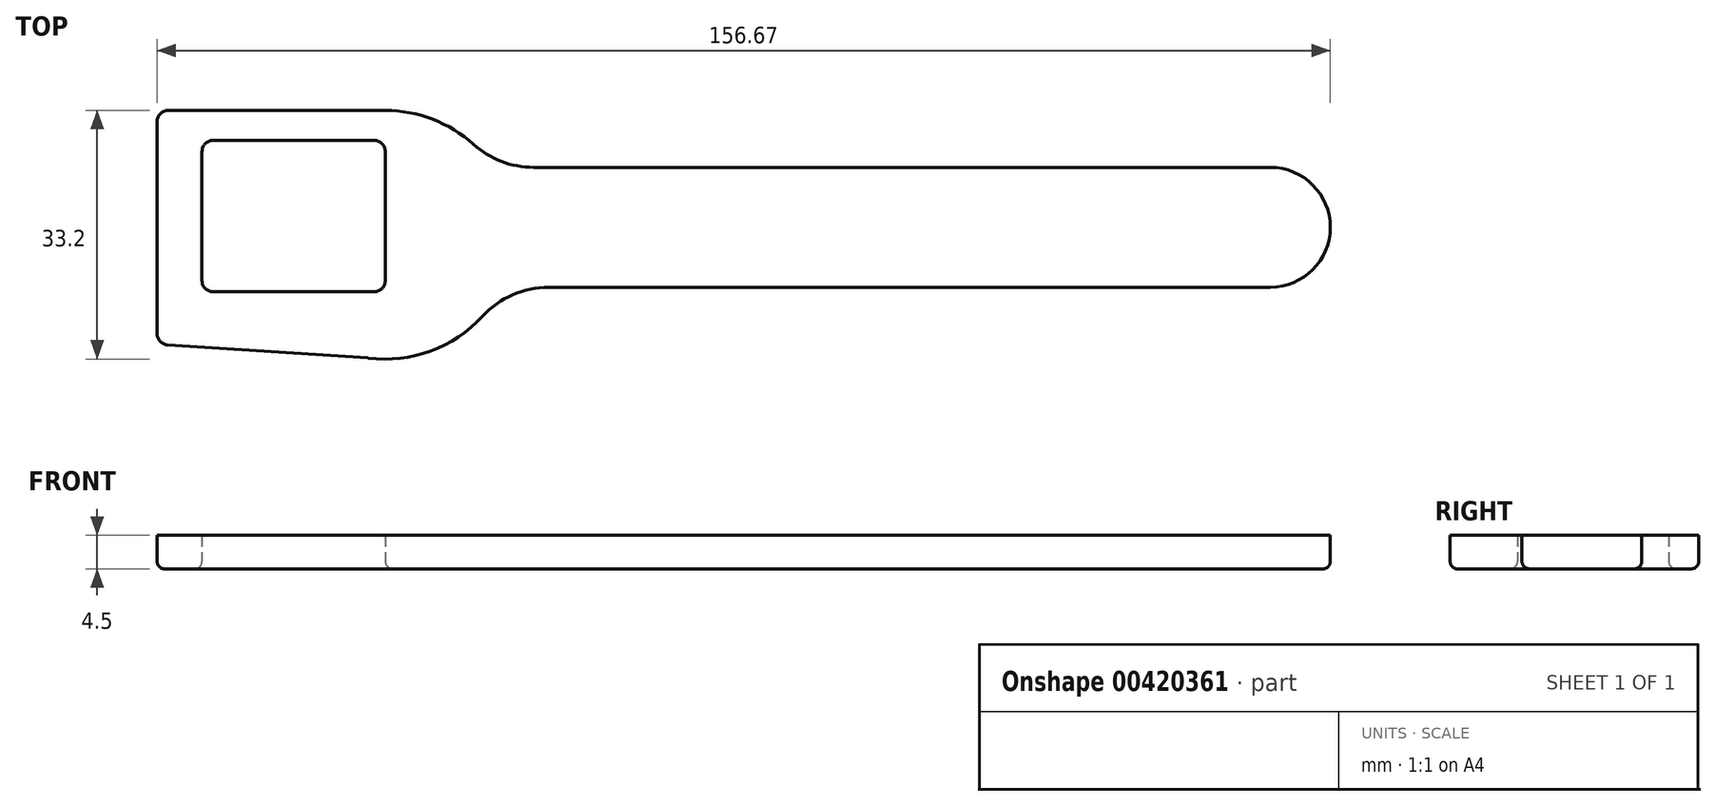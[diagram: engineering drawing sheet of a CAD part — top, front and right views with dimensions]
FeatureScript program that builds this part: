
annotation { "Feature Type Name" : "Feature", "Feature Type Description" : "" }
export const myFeature = defineFeature(function(context is Context, id is Id, definition is map)
    precondition{}
    {
        {
            var Q0;
            Q0=qCreatedBy(makeId("Top.planeOp"),FACE);
            var sketch = newSketch(context, id + "F0", { "sketchPlane" : qUnion([Q0])});
            skArc(sketch, "E0", {"start": v(-72.82, -17.45) * mm, "mid": v(-62.33, -15.58) * mm, "end": v(-54.85, -8) * mm});
            skLineSegment(sketch, "E1", {"start": v(59.4, -20.35) * mm, "end": v(59.4, 16.2) * mm, "construction": true});
            skLineSegment(sketch, "E2", {"start": v(-88.12, 35.8) * mm, "end": v(-88.12, -38.11) * mm, "construction": true});
            skLineSegment(sketch, "E3.top", {"start": v(-70.52, -17.6) * mm, "end": v(-50.32, -17.6) * mm, "construction": true});
            skLineSegment(sketch, "E3.right", {"start": v(-50.32, 17.6) * mm, "end": v(-50.32, -17.6) * mm, "construction": true});
            skLineSegment(sketch, "E4.top", {"start": v(-70.52, -8.6) * mm, "end": v(-88.12, -8.6) * mm});
            skLineSegment(sketch, "E5", {"start": v(-63.17, 15.6) * mm, "end": v(-90.72, 15.6) * mm});
            skLineSegment(sketch, "E6", {"start": v(-70.52, -17.6) * mm, "end": v(-101, -15.6) * mm});
            skLineSegment(sketch, "E7", {"start": v(-98.89, 0) * mm, "end": v(66.7, 0) * mm, "construction": true});
            skArc(sketch, "E8", {"start": v(47.67, -8) * mm, "mid": v(55.67, 0) * mm, "end": v(47.67, 8) * mm});
            skLineSegment(sketch, "E9", {"start": v(47.67, 8) * mm, "end": v(-50.32, 8) * mm});
            skLineSegment(sketch, "E10", {"start": v(47.67, -8) * mm, "end": v(-54.85, -8) * mm});
            skArc(sketch, "E11.trimOffspring", {"start": v(-56.04, 8) * mm, "mid": v(-62.35, 13.58) * mm, "end": v(-70.52, 15.6) * mm});
            skLineSegment(sketch, "E12", {"start": v(-97.29, 15.6) * mm, "end": v(-46.92, 15.6) * mm, "construction": true});
            skLineSegment(sketch, "E13", {"start": v(-50.32, 8) * mm, "end": v(-56.04, 8) * mm});
            skLineSegment(sketch, "E14.bottom", {"start": v(-90.72, 15.6) * mm, "end": v(-95, 15.6) * mm});
            skLineSegment(sketch, "E15.bottom", {"start": v(-95, 15.6) * mm, "end": v(-101, 15.6) * mm});
            skLineSegment(sketch, "E15.left", {"start": v(-95, 11.6) * mm, "end": v(-95, -8.6) * mm});
            skLineSegment(sketch, "E15.right", {"start": v(-101, 15.6) * mm, "end": v(-101, -15.6) * mm});
            skLineSegment(sketch, "E16", {"start": v(-95, 11.6) * mm, "end": v(-70.52, 11.6) * mm});
            skLineSegment(sketch, "E17", {"start": v(-88.12, -8.6) * mm, "end": v(-95, -8.6) * mm});
            skLineSegment(sketch, "E18", {"start": v(-70.52, 11.6) * mm, "end": v(-70.52, -8.6) * mm});
            skSolve(sketch);
        }
        {
            var Q0;
            Q0=qSketchRegion(id+"F0",true);
            extrude(context, id + "F1", {"entities" : qUnion([Q0]), "depth" : 4.5 * mm});
        }
        {
            var Q0;
            Q0=makeQuery(id+"F1.opExtrude","SWEPT_EDGE",EDGE,{"disambiguationData":[OSD([sQuery(id+"F0.wireOp",EDGE,"E0"),sQuery(id+"F0.wireOp",EDGE,"E6")])]});
            var Q1;
            Q1=makeQuery(id+"F1.opExtrude","SWEPT_EDGE",EDGE,{"disambiguationData":[OSD([sQuery(id+"F0.wireOp",EDGE,"E5"),sQuery(id+"F0.wireOp",EDGE,"E11.trimOffspring")])]});
            var Q2;
            Q2=makeQuery(id+"F1.opExtrude","SWEPT_EDGE",EDGE,{"disambiguationData":[OSD([sQuery(id+"F0.wireOp",EDGE,"E4.top"),sQuery(id+"F0.wireOp",EDGE,"MguvdN41-JgFZ-7uOa-Q9f6-B0BVnigIjYcD")])]});
            var Q3;
            Q3=makeQuery(id+"F1.opExtrude","SWEPT_EDGE",EDGE,{"disambiguationData":[OSD([sQuery(id+"F0.wireOp",EDGE,"E4.top"),sQuery(id+"F0.wireOp",EDGE,"MguvdN41-JgFZ-7uOa-Q9f6-B0BVnigIjYcD")])]});
            var Q4;
            Q4=makeQuery(id+"F1.opExtrude","SWEPT_EDGE",EDGE,{"disambiguationData":[OSD([sQuery(id+"F0.wireOp",EDGE,"MguvdN41-JgFZ-7uOa-Q9f6-B0BVnigIjYcD"),sQuery(id+"F0.wireOp",EDGE,"E16")])]});
            var Q5;
            Q5=makeQuery(id+"F1.opExtrude","SWEPT_EDGE",EDGE,{"disambiguationData":[OSD([sQuery(id+"F0.wireOp",EDGE,"E4.top"),sQuery(id+"F0.wireOp",EDGE,"MguvdN41-JgFZ-7uOa-Q9f6-B0BVnigIjYcD")])]});
            var Q6;
            Q6=makeQuery(id+"F1.opExtrude","SWEPT_EDGE",EDGE,{"disambiguationData":[OSD([sQuery(id+"F0.wireOp",EDGE,"E15.left"),sQuery(id+"F0.wireOp",EDGE,"E16")])]});
            var Q7;
            Q7=makeQuery(id+"F1.opExtrude","SWEPT_EDGE",EDGE,{"disambiguationData":[OSD([sQuery(id+"F0.wireOp",EDGE,"E15.left"),sQuery(id+"F0.wireOp",EDGE,"E17")])]});
            var Q8;
            Q8=makeQuery(id+"F1.opExtrude","SWEPT_EDGE",EDGE,{"disambiguationData":[OSD([sQuery(id+"F0.wireOp",EDGE,"E15.bottom"),sQuery(id+"F0.wireOp",EDGE,"E15.right")])]});
            var Q9;
            Q9=makeQuery(id+"F1.opExtrude","SWEPT_EDGE",EDGE,{"disambiguationData":[OSD([sQuery(id+"F0.wireOp",EDGE,"E15.right"),sQuery(id+"F0.wireOp",EDGE,"sJWdUn0g-EcUp-Njcm-fq6M-NqAFcOtqrBxr")])]});
            fillet(context, id + "F2", {"entities" : qUnion([Q0, Q1, Q2, Q3, Q4, Q5, Q6, Q7, Q8, Q9]), "radius" : 1.5 * mm, "tangentPropagation" : true, "allowEdgeOverflow" : false});
        }
        {
            var Q0;
            Q0=makeQuery(id+"F1.opExtrude","SWEPT_EDGE",EDGE,{"disambiguationData":[OSD([sQuery(id+"F0.wireOp",EDGE,"E9"),sQuery(id+"F0.wireOp",EDGE,"E11.trimOffspring")])]});
            var Q1;
            Q1=makeQuery(id+"F1.opExtrude","SWEPT_EDGE",EDGE,{"disambiguationData":[OSD([sQuery(id+"F0.wireOp",EDGE,"E0"),sQuery(id+"F0.wireOp",EDGE,"E10")])]});
            fillet(context, id + "F3", {"entities" : qUnion([Q0, Q1]), "radius" : 12 * mm, "tangentPropagation" : true, "allowEdgeOverflow" : false});
        }
        {
            var Q0;
            Q0=makeQuery(id+"F1.opExtrude","CAP_FACE",FACE,{"disambiguationData":[OSD([sQuery(id+"F0.wireOp",EDGE,"E0"),sQuery(id+"F0.wireOp",EDGE,"gCLExgJr-G97b-xlZ5-FV4S-7oY0YXoP74uk.top"),sQuery(id+"F0.wireOp",EDGE,"E4.top"),sQuery(id+"F0.wireOp",EDGE,"E5"),sQuery(id+"F0.wireOp",EDGE,"JTNi2FiC-B9Hd-yy0C-NibE-VtpdYRL0dKmn"),sQuery(id+"F0.wireOp",EDGE,"b8165475-47af-4af3-b4ca-044acb1de50d.trimOffspring"),sQuery(id+"F0.wireOp",EDGE,"E6"),sQuery(id+"F0.wireOp",EDGE,"MguvdN41-JgFZ-7uOa-Q9f6-B0BVnigIjYcD"),sQuery(id+"F0.wireOp",EDGE,"E8"),sQuery(id+"F0.wireOp",EDGE,"E9"),sQuery(id+"F0.wireOp",EDGE,"E10"),sQuery(id+"F0.wireOp",EDGE,"E11.trimOffspring"),sQuery(id+"F0.wireOp",EDGE,"E13")])],"isStart":true});
            fillet(context, id + "F4", {"entities" : qUnion([Q0]), "radius" : 1 * mm, "tangentPropagation" : true, "allowEdgeOverflow" : false});
        }
    });
